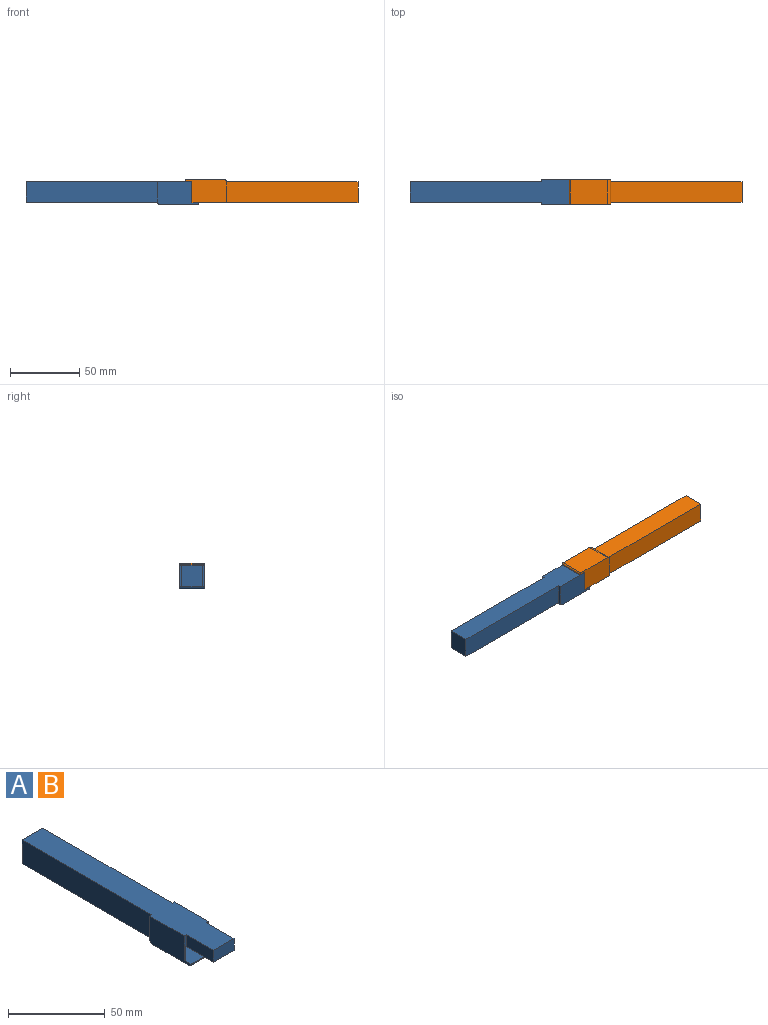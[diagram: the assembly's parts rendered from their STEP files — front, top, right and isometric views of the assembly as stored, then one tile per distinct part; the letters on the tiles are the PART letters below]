
ASSEMBLY  parts=2 mates=1
PART A: 25 faces, bbox 18x140x16.9 mm
  f0: plane 15.5x1.5mm, normal (0,-1,0), area 19mm2, adj f2,f8,f13,f14,f15,f20
  f1: plane 14.94x1.5mm, normal (0,1,0), area 22.4mm2, adj f4,f8,f20,f22
  f2: plane 40x7.5mm, normal (1,0,0), area 159.4mm2, adj f0,f8,f9,f10,f11,f13
  f3: plane 40x7.5mm, normal (-1,0,0), area 159.4mm2, adj f8,f9,f10,f11,f12,f17
  f4: plane 95x15mm, normal (1,0,0), area 1425mm2, adj f1,f6,f7,f8,f22
  f5: plane 95x15mm, normal (-1,0,0), area 1425mm2, adj f6,f7,f8,f21,f22
  f6: plane 15x15mm, normal (0,1,0), area 225mm2, adj f4,f5,f7,f8
  f7: plane 95x15mm, normal (0,0,-1), area 1425mm2, adj f4,f5,f6,f22
  f8: plane 140x18mm, normal (0,0,1), area 2175mm2, adj f0,f1,f2,f3,f4,f5,f6,f10
  f9: plane 40x15mm, normal (0,0,-1), area 600mm2, adj f2,f3,f10,f11
  f10: plane 15x7.5mm, normal (0,-1,0), area 112.5mm2, adj f2,f3,f8,f9
  f11: plane 16x8.47mm, normal (0,-1,0), area 128.5mm2, adj f2,f3,f9,f13,f14,f15,f16,f17
  f12: plane 15.5x1.5mm, normal (0,-1,0), area 19mm2, adj f3,f8,f15,f16,f17,f18
  f13: plane 20x0.5mm, normal (0,0,-1), area 10mm2, adj f0,f2,f11,f14
  f14: plane 20x8.47mm, normal (-1,0,0), area 169.4mm2, adj f0,f11,f13,f15
  f15: plane 25x18mm, normal (0,0,1), area 410mm2, adj f0,f11,f12,f14,f16,f18,f20,f23
  f16: plane 20x8.47mm, normal (1,0,0), area 169.4mm2, adj f11,f12,f15,f17
  f17: plane 20x0.5mm, normal (0,0,-1), area 10mm2, adj f3,f11,f12,f16
  f18: plane 30x16.94mm, normal (-1,0,0), area 429.5mm2, adj f8,f12,f15,f19,f21,f22,f23,f24
  f19: plane 27x18mm, normal (0,0,-1), area 486mm2, adj f18,f20,f22,f24
  f20: plane 30x16.94mm, normal (1,0,0), area 429.5mm2, adj f0,f1,f8,f15,f19,f22,f23,f24
  f21: plane 14.94x1.5mm, normal (0,1,0), area 22.4mm2, adj f5,f8,f18,f22
  f22: cylinder r=2mm len=18mm, axis (1,0,0), area 55.6mm2, adj f1,f4,f5,f7,f18,f19,f20,f21
  f23: plane 18x0.44mm, normal (0,-1,0), area 7.8mm2, adj f15,f18,f20,f24
  f24: cylinder r=1mm len=18mm, axis (-1,0,0), area 28.3mm2, adj f18,f19,f20,f23
PART B: same geometry as A
PLACE A rot(axis=(0,0,1),90deg) t=(-11.63,61.39,-2.47)mm
PLACE B rot(axis=(0.71,0.71,0),180deg) t=(-11.63,61.39,12.3)mm
MATE fastened A.f10 <-> B.f11  axis (1,0,0) through (8.37,61.39,8.78)mm
